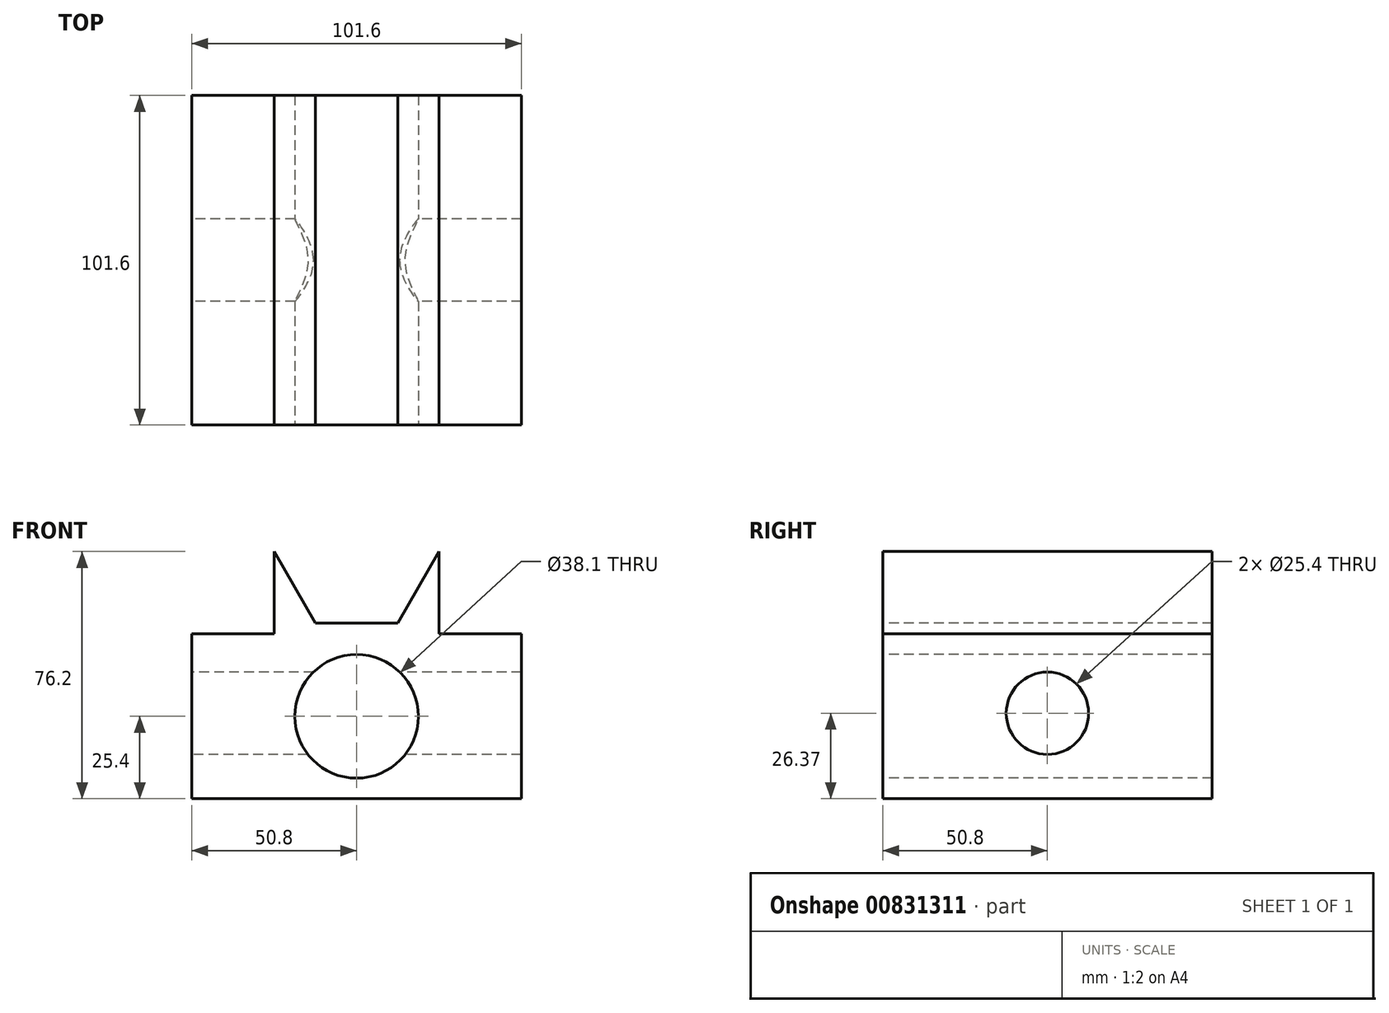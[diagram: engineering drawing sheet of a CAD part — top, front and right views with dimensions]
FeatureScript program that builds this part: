
annotation { "Feature Type Name" : "Feature", "Feature Type Description" : "" }
export const myFeature = defineFeature(function(context is Context, id is Id, definition is map)
    precondition{}
    {
        {
            var Q0;
            Q0=qCreatedBy(makeId("Front.planeOp"),FACE);
            var sketch = newSketch(context, id + "F0", { "sketchPlane" : qUnion([Q0])});
            skLineSegment(sketch, "E0.bottom", {"start": v(0, 0) * mm, "end": v(101.6, 0) * mm});
            skLineSegment(sketch, "E0.top", {"start": v(0, 50.8) * mm, "end": v(101.6, 50.8) * mm});
            skLineSegment(sketch, "E0.left", {"start": v(0, 0) * mm, "end": v(0, 50.8) * mm});
            skLineSegment(sketch, "E0.right", {"start": v(101.6, 0) * mm, "end": v(101.6, 50.8) * mm});
            skSolve(sketch);
        }
        {
            var Q0;
            Q0=makeQuery(id+"F0.imprint","IMPRINT",FACE,{"disambiguationData":[TD([[makeQuery(id+"F0.imprint","IMPRINT",EDGE,{"derivedFrom":sQuery(id+"F0.wireOp",EDGE,"E0.bottom")}),1.0]])]});
            extrude(context, id + "F1", {"entities" : qUnion([Q0]), "depth" : 101.6 * mm, "offsetDistance" : 25.4 * mm});
        }
        {
            var Q0;
            Q0=makeQuery(id+"F1.opExtrude","SWEPT_FACE",FACE,{"disambiguationData":[OSD([sQuery(id+"F0.wireOp",EDGE,"E0.top")])]});
            var sketch = newSketch(context, id + "F2", { "sketchPlane" : qUnion([Q0])});
            skLineSegment(sketch, "E1", {"start": v(50.8, 0) * mm, "end": v(50.8, -101.6) * mm, "construction": true});
            skLineSegment(sketch, "E2", {"start": v(25.4, 0) * mm, "end": v(25.4, -101.6) * mm});
            skLineSegment(sketch, "E3", {"start": v(76.2, 0) * mm, "end": v(76.2, -101.6) * mm});
            skSolve(sketch);
        }
        {
            var Q0;
            {var subQ0=sQuery(id+"F2.wireOp",EDGE,"E2");Q0=makeQuery(id+"F2.imprint","IMPRINT",FACE,{"disambiguationData":[TD([[makeQuery(id+"F2.imprint","IMPRINT",EDGE,{"derivedFrom":subQ0}),1.0]])]});}
            extrude(context, id + "F3", {"entities" : qUnion([Q0]), "operationType" : NewBodyOperationType.ADD, "depth" : 25.4 * mm, "offsetDistance" : 25.4 * mm});
        }
        {
            var Q0;
            {var subQ0=sQuery(id+"F0.wireOp",EDGE,"E0.top");var subQ1=makeQuery(id+"F1.opExtrude","CAP_EDGE",EDGE,{"disambiguationData":[OSD([subQ0])],"isStart":false});Q0=makeQuery(id+"F3.boolean.opBoolean","MERGE",FACE,{"derivedFrom":[makeQuery(id+"F1.opExtrude","CAP_FACE",FACE,{"disambiguationData":[OSD([sQuery(id+"F0.wireOp",EDGE,"E0.bottom"),subQ0,sQuery(id+"F0.wireOp",EDGE,"E0.left"),sQuery(id+"F0.wireOp",EDGE,"E0.right")])],"isStart":false}),makeQuery(id+"F3.opExtrude","SWEPT_FACE",FACE,{"disambiguationData":[OSD([subQ0]),TDD([makeQuery(id+"F2.imprint","IMPRINT",EDGE,{"disambiguationData":[TD([[makeQuery(id+"F2.imprint","INTERSECT",VERTEX,{"derivedFrom":[subQ1,sQuery(id+"F2.wireOp",EDGE,"E2")]}),-1.0]])],"derivedFrom":subQ1})])]})]});}
            var sketch = newSketch(context, id + "F4", { "sketchPlane" : qUnion([Q0])});
            skLineSegment(sketch, "E4", {"start": v(25.4, 76.2) * mm, "end": v(38.1, 54.2) * mm});
            skLineSegment(sketch, "E5", {"start": v(38.1, 54.2) * mm, "end": v(63.5, 54.2) * mm});
            skLineSegment(sketch, "E6", {"start": v(63.5, 54.2) * mm, "end": v(76.2, 76.2) * mm});
            skLineSegment(sketch, "E7", {"start": v(50.8, 76.2) * mm, "end": v(50.8, 0) * mm, "construction": true});
            skSolve(sketch);
        }
        {
            var Q0;
            Q0=makeQuery(id+"F4.imprint","IMPRINT",FACE,{"disambiguationData":[TD([[makeQuery(id+"F4.imprint","IMPRINT",EDGE,{"derivedFrom":sQuery(id+"F4.wireOp",EDGE,"E4")}),1.0]])]});
            extrude(context, id + "F5", {"entities" : qUnion([Q0]), "operationType" : NewBodyOperationType.REMOVE, "oppositeDirection" : true, "depth" : 101.6 * mm, "offsetDistance" : 25.4 * mm});
        }
        {
            var Q0;
            {var subQ0=sQuery(id+"F0.wireOp",EDGE,"E0.top");var subQ1=makeQuery(id+"F1.opExtrude","CAP_EDGE",EDGE,{"disambiguationData":[OSD([subQ0])],"isStart":false});Q0=makeQuery(id+"F3.boolean.opBoolean","MERGE",FACE,{"derivedFrom":[makeQuery(id+"F1.opExtrude","CAP_FACE",FACE,{"disambiguationData":[OSD([sQuery(id+"F0.wireOp",EDGE,"E0.bottom"),subQ0,sQuery(id+"F0.wireOp",EDGE,"E0.left"),sQuery(id+"F0.wireOp",EDGE,"E0.right")])],"isStart":false}),makeQuery(id+"F3.opExtrude","SWEPT_FACE",FACE,{"disambiguationData":[OSD([subQ0]),TDD([makeQuery(id+"F2.imprint","IMPRINT",EDGE,{"disambiguationData":[TD([[makeQuery(id+"F2.imprint","INTERSECT",VERTEX,{"derivedFrom":[subQ1,sQuery(id+"F2.wireOp",EDGE,"E2")]}),-1.0]])],"derivedFrom":subQ1})])]})]});}
            var sketch = newSketch(context, id + "F6", { "sketchPlane" : qUnion([Q0])});
            skLineSegment(sketch, "E8", {"start": v(50.8, 54.2) * mm, "end": v(50.8, 0) * mm, "construction": true});
            skLineSegment(sketch, "E9", {"start": v(0, 25.4) * mm, "end": v(101.6, 25.4) * mm, "construction": true});
            skCircle(sketch, "E10", {"center": v(50.8, 25.4) * mm, "radius": 19.05 * mm});
            skSolve(sketch);
        }
        {
            var Q0;
            Q0=makeQuery(id+"F6.imprint","IMPRINT",FACE,{"disambiguationData":[TD([[makeQuery(id+"F6.imprint","IMPRINT",EDGE,{"derivedFrom":sQuery(id+"F6.wireOp",EDGE,"E10")}),1.0]])]});
            extrude(context, id + "F7", {"entities" : qUnion([Q0]), "operationType" : NewBodyOperationType.REMOVE, "oppositeDirection" : true, "depth" : 101.6 * mm, "offsetDistance" : 25.4 * mm});
        }
        {
            var Q0;
            Q0=makeQuery(id+"F1.opExtrude","SWEPT_FACE",FACE,{"disambiguationData":[OSD([sQuery(id+"F0.wireOp",EDGE,"E0.left")])]});
            var sketch = newSketch(context, id + "F8", { "sketchPlane" : qUnion([Q0])});
            skCircle(sketch, "E11", {"center": v(50.8, 26.37) * mm, "radius": 12.7 * mm});
            skPoint(sketch, "E11.centerSnap0", {"position": v(50.8, 0) * mm});
            skSolve(sketch);
        }
        {
            var Q0;
            Q0=makeQuery(id+"F8.imprint","IMPRINT",FACE,{"disambiguationData":[TD([[makeQuery(id+"F8.imprint","IMPRINT",EDGE,{"derivedFrom":sQuery(id+"F8.wireOp",EDGE,"E11")}),1.0]])]});
            extrude(context, id + "F9", {"entities" : qUnion([Q0]), "operationType" : NewBodyOperationType.REMOVE, "oppositeDirection" : true, "depth" : 101.6 * mm, "offsetDistance" : 25.4 * mm});
        }
    });
